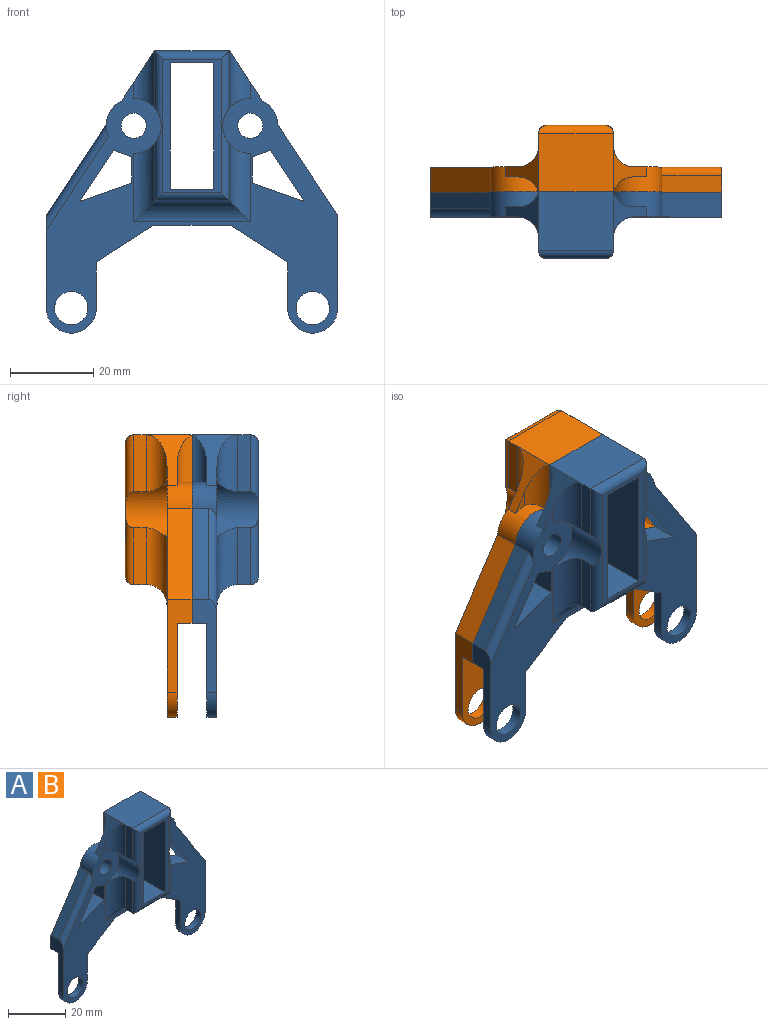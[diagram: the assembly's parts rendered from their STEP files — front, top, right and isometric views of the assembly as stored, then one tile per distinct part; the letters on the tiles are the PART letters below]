
ASSEMBLY  parts=2 mates=1
PART A: 60 faces, bbox 71.7x16x67.8 mm
  f0: plane 4.79x3.15mm, normal (0,1,0), area 6mm2, adj f38,f39,f54
  f1: plane 4.79x3.15mm, normal (0,1,0), area 6mm2, adj f25,f26,f52
  f2: plane 70x31.8mm, normal (0,1,0), area 782.3mm2, adj f3,f28,f29,f30,f31,f32,f33,f34
  f3: plane 18x3.6mm, normal (0,0,-1), area 64.8mm2, adj f2,f17,f46,f47
  f4: plane 18x14mm, normal (0,0,1), area 252mm2, adj f5,f15,f17,f25,f39,f57
  f5: plane 13.68x3mm, normal (-1,0,0), area 41.1mm2, adj f4,f6,f48,f56
  f6: cylinder r=6.61mm len=13.21mm, axis (0,1,0), area 104.6mm2, adj f5,f7,f18,f48,f51,f56
  f7: plane 13.68x3mm, normal (-1,0,0), area 41.1mm2, adj f6,f8,f51,f56
  f8: plane 18x3mm, normal (0,0,-1), area 54mm2, adj f7,f9,f50,f58
  f9: plane 13.68x3mm, normal (1,0,0), area 41.1mm2, adj f8,f10,f49,f59
  f10: cylinder r=6.61mm len=13.21mm, axis (0,1,0), area 104.6mm2, adj f9,f15,f18,f49,f53,f59
  f11: plane 30.5x16mm, normal (1,0,0), area 488mm2, adj f12,f14,f16,f17
  f12: plane 16x10.5mm, normal (0,0,-1), area 168mm2, adj f11,f13,f16,f17
  f13: plane 30.5x16mm, normal (-1,0,0), area 488mm2, adj f12,f14,f16,f17
  f14: plane 16x10.5mm, normal (0,0,1), area 168mm2, adj f11,f13,f16,f17
  f15: plane 13.68x3mm, normal (1,0,0), area 41.1mm2, adj f4,f10,f53,f59
  f16: plane 32x14mm, normal (0,-1,0), area 127.7mm2, adj f11,f12,f13,f14,f56,f57,f58,f59
  f17: plane 70x45.29mm, normal (0,1,0), area 1124.6mm2, adj f3,f4,f11,f12,f13,f14,f19,f20
  f18: plane 70x60.19mm, normal (0,-1,0), area 1294.6mm2, adj f6,f10,f19,f20,f21,f22,f23,f24
  f19: plane 12.53x6mm, normal (-0.34,0,0.94), area 79.8mm2, adj f17,f18,f20,f45
  f20: plane 12.36x8.12mm, normal (0.84,0,-0.55), area 88.7mm2, adj f17,f18,f19,f21
  f21: plane 6x4.41mm, normal (-0.33,0,-0.94), area 28.1mm2, adj f17,f18,f20,f45
  f22: plane 12.53x6mm, normal (0.34,0,0.94), area 79.8mm2, adj f17,f18,f23,f41
  f23: plane 6.32x6mm, normal (1,0,0), area 37.9mm2, adj f17,f18,f22,f24
  f24: plane 6x4.41mm, normal (0.33,0,-0.94), area 28.1mm2, adj f17,f18,f23,f41
  f25: plane 12.09x11mm, normal (-0.84,0,0.55), area 52.8mm2, adj f1,f4,f18,f26,f48,f52
  f26: cylinder r=6.61mm len=11.61mm, axis (0,1,0), area 68.8mm2, adj f1,f17,f18,f25,f27,f52,f55
  f27: plane 21.91x14.4mm, normal (-0.84,0,0.55), area 104.9mm2, adj f17,f26,f28,f55
  f28: plane 22.25x6mm, normal (-1,0,0), area 72.5mm2, adj f2,f17,f18,f27,f29,f46,f55
  f29: cylinder r=6mm len=12mm, axis (0,1,0), area 45.2mm2, adj f2,f18,f28,f30
  f30: plane 11.09x2.4mm, normal (1,0,0), area 26.6mm2, adj f2,f18,f29,f31
  f31: plane 13.83x8.84mm, normal (0.54,0,-0.84), area 39.4mm2, adj f2,f18,f30,f32
  f32: plane 18.34x2.4mm, normal (0,0,-1), area 44mm2, adj f2,f18,f31,f33
  f33: plane 13.83x8.84mm, normal (-0.54,0,-0.84), area 39.4mm2, adj f2,f18,f32,f34
  f34: plane 11.09x2.4mm, normal (-1,0,0), area 26.6mm2, adj f2,f18,f33,f35
  f35: cylinder r=6mm len=12mm, axis (0,1,0), area 45.2mm2, adj f2,f18,f34,f36
  f36: plane 22.25x6mm, normal (1,0,0), area 74mm2, adj f2,f17,f18,f35,f37,f47
  f37: plane 21.91x14.4mm, normal (0.84,0,0.55), area 157.3mm2, adj f17,f18,f36,f38
  f38: cylinder r=6.61mm len=11.6mm, axis (0,1,0), area 67.3mm2, adj f0,f17,f18,f37,f39,f54
  f39: plane 12.09x11mm, normal (0.84,0,0.55), area 52.8mm2, adj f0,f4,f18,f38,f53,f54
  f40: cylinder r=3mm len=6mm, axis (0,1,0), area 113.1mm2, adj f17,f18
  f41: plane 12.36x8.12mm, normal (-0.84,0,-0.55), area 88.7mm2, adj f17,f18,f22,f24
  f42: cylinder r=3mm len=6mm, axis (0,1,0), area 113.1mm2, adj f17,f18
  f43: cylinder r=4mm len=8mm, axis (0,1,0), area 60.3mm2, adj f2,f18
  f44: cylinder r=4mm len=8mm, axis (0,1,0), area 60.3mm2, adj f2,f18
  f45: plane 6.32x6mm, normal (-1,0,0), area 37.9mm2, adj f17,f18,f19,f21
  f46: plane 26x9.29mm, normal (0.34,0,-0.94), area 99.4mm2, adj f2,f3,f17,f28
  f47: plane 26x9.29mm, normal (-0.34,0,-0.94), area 99.4mm2, adj f2,f3,f17,f36
  f48: cylinder r=5mm len=13.68mm, axis (0,0,-1), area 76.3mm2, adj f5,f6,f18,f25
  f49: cylinder r=5mm len=18.68mm, axis (0,0,1), area 112.3mm2, adj f9,f10,f18,f50
  f50: cylinder r=5mm len=28mm, axis (1,0,0), area 169.9mm2, adj f8,f18,f49,f51
  f51: cylinder r=5mm len=18.68mm, axis (0,0,-1), area 112.3mm2, adj f6,f7,f18,f50
  f52: cylinder r=5mm len=13.68mm, axis (0,0,-1), area 59.8mm2, adj f1,f17,f25,f26
  f53: cylinder r=5mm len=13.68mm, axis (0,0,1), area 76.3mm2, adj f10,f15,f18,f39
  f54: cylinder r=5mm len=13.68mm, axis (0,0,-1), area 59.8mm2, adj f0,f17,f38,f39
  f55: cylinder r=2mm len=25.55mm, axis (0.55,0,0.84), area 83mm2, adj f18,f26,f27,f28
  f56: cylinder r=2mm len=36mm, axis (0,0,1), area 90mm2, adj f5,f6,f7,f16,f57,f58
  f57: cylinder r=2mm len=18mm, axis (1,0,0), area 52mm2, adj f4,f16,f56,f59
  f58: cylinder r=2mm len=18mm, axis (-1,0,0), area 52mm2, adj f8,f16,f56,f59
  f59: cylinder r=2mm len=36mm, axis (0,0,-1), area 90mm2, adj f9,f10,f15,f16,f57,f58
PART B: same geometry as A
PLACE A t=(-13.81,-13.14,-1.02)mm
PLACE B rot(axis=(0,0,1),180deg) t=(-13.81,-13.14,-1.02)mm
MATE fastened B.f40 <-> A.f42  axis (0,-1,0) through (0.19,-13.14,-1.02)mm
